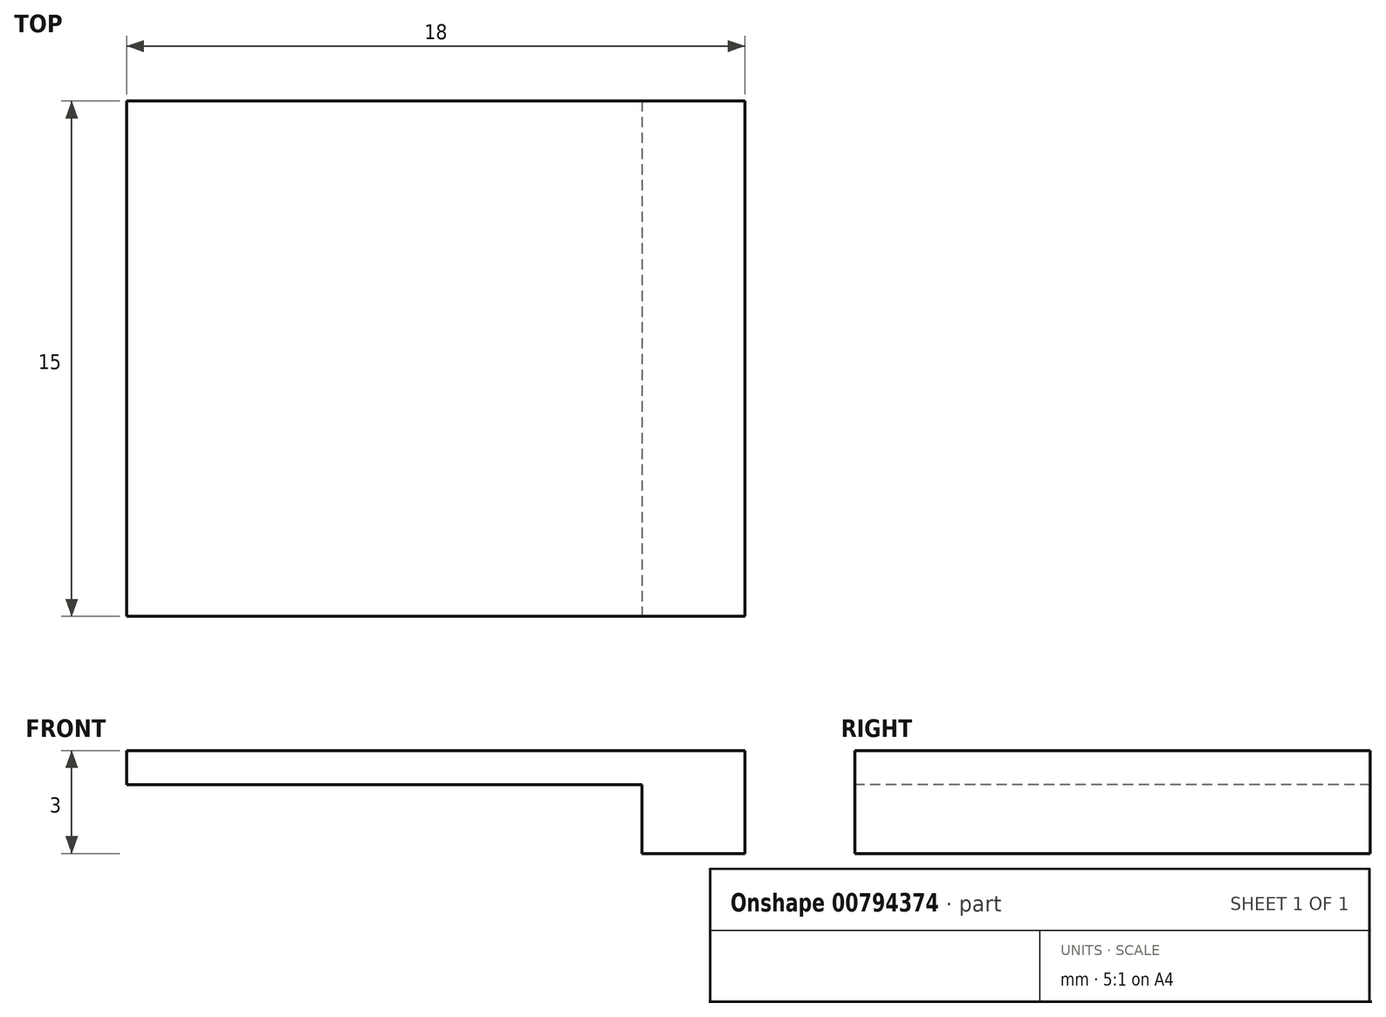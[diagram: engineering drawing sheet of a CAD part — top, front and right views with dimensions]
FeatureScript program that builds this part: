
annotation { "Feature Type Name" : "Feature", "Feature Type Description" : "" }
export const myFeature = defineFeature(function(context is Context, id is Id, definition is map)
    precondition{}
    {
        {
            var Q0;
            Q0=qCreatedBy(makeId("Top.planeOp"),FACE);
            var sketch = newSketch(context, id + "F0", { "sketchPlane" : qUnion([Q0])});
            skLineSegment(sketch, "E0.bottom", {"start": v(1.5, -7.5) * mm, "end": v(-1.5, -7.5) * mm});
            skLineSegment(sketch, "E0.top", {"start": v(1.5, 7.5) * mm, "end": v(-1.5, 7.5) * mm});
            skLineSegment(sketch, "E0.left", {"start": v(1.5, -7.5) * mm, "end": v(1.5, 7.5) * mm});
            skLineSegment(sketch, "E0.right", {"start": v(-1.5, -7.5) * mm, "end": v(-1.5, 7.5) * mm});
            skPoint(sketch, "E0.middle", {"position": v(0, 0) * mm});
            skSolve(sketch);
        }
        {
            var Q0;
            Q0=makeQuery(id+"F0.imprint","IMPRINT",FACE,{"disambiguationData":[TD([[makeQuery(id+"F0.imprint","IMPRINT",EDGE,{"derivedFrom":sQuery(id+"F0.wireOp",EDGE,"E0.bottom")}),-1.0]])]});
            extrude(context, id + "F1", {"entities" : qUnion([Q0]), "depth" : 3 * mm, "offsetDistance" : 25 * mm});
        }
        {
            var Q0;
            Q0=makeQuery(id+"F1.opExtrude","SWEPT_FACE",FACE,{"disambiguationData":[OSD([sQuery(id+"F0.wireOp",EDGE,"E0.right")])]});
            var sketch = newSketch(context, id + "F2", { "sketchPlane" : qUnion([Q0])});
            skLineSegment(sketch, "E1.bottom", {"start": v(-7.5, 3) * mm, "end": v(7.5, 3) * mm});
            skLineSegment(sketch, "E1.top", {"start": v(-7.5, 2) * mm, "end": v(7.5, 2) * mm});
            skLineSegment(sketch, "E1.left", {"start": v(-7.5, 3) * mm, "end": v(-7.5, 2) * mm});
            skLineSegment(sketch, "E1.right", {"start": v(7.5, 3) * mm, "end": v(7.5, 2) * mm});
            skSolve(sketch);
        }
        {
            var Q0;
            Q0=makeQuery(id+"F2.imprint","IMPRINT",FACE,{"disambiguationData":[TD([[makeQuery(id+"F2.imprint","IMPRINT",EDGE,{"derivedFrom":sQuery(id+"F2.wireOp",EDGE,"E1.bottom")}),1.0]])]});
            extrude(context, id + "F3", {"entities" : qUnion([Q0]), "operationType" : NewBodyOperationType.ADD, "depth" : 15 * mm, "offsetDistance" : 25 * mm});
        }
    });
